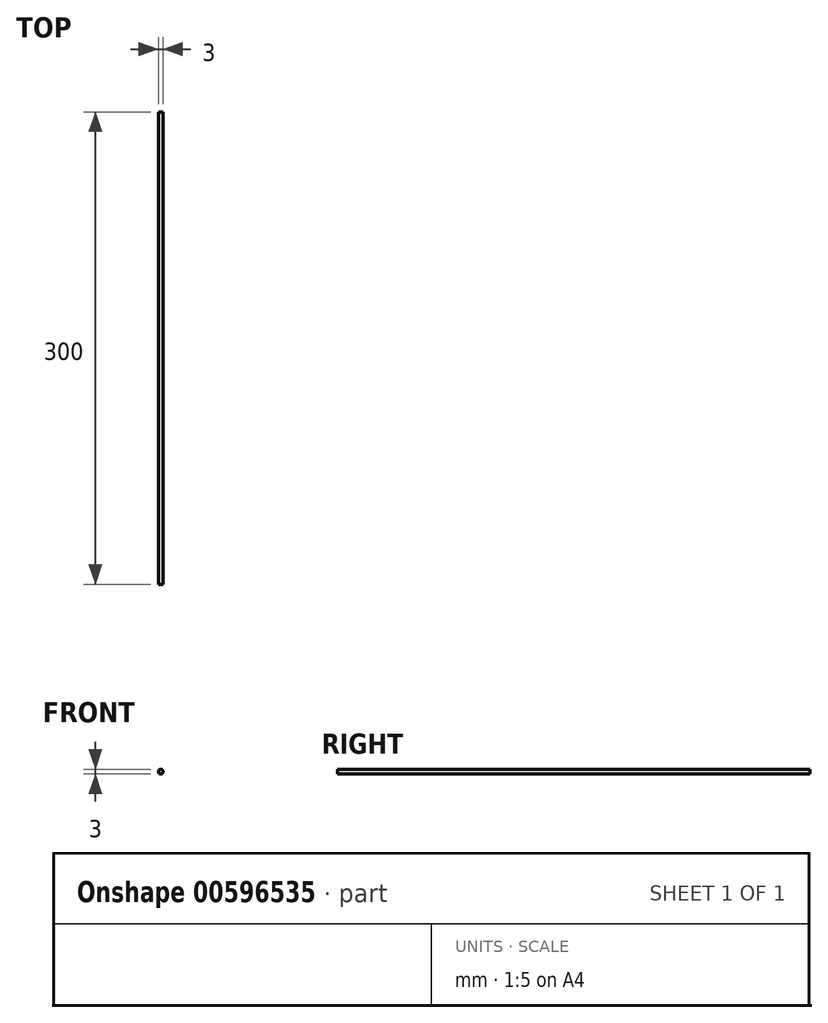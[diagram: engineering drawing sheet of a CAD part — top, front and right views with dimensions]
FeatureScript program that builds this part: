
annotation { "Feature Type Name" : "Feature", "Feature Type Description" : "" }
export const myFeature = defineFeature(function(context is Context, id is Id, definition is map)
    precondition{}
    {
        {
            var Q0;
            Q0=qCreatedBy(makeId("Front.planeOp"),FACE);
            var sketch = newSketch(context, id + "F0", { "sketchPlane" : qUnion([Q0])});
            skCircle(sketch, "E0", {"center": v(0, 0) * mm, "radius": 1.5 * mm});
            skSolve(sketch);
        }
        {
            var Q0;
            Q0=makeQuery(id+"F0.imprint","IMPRINT",FACE,{"disambiguationData":[TD([[makeQuery(id+"F0.imprint","IMPRINT",EDGE,{"derivedFrom":sQuery(id+"F0.wireOp",EDGE,"E0")}),1.0]])]});
            extrude(context, id + "F1", {"entities" : qUnion([Q0]), "depth" : 300 * mm, "offsetDistance" : 25 * mm});
        }
    });
